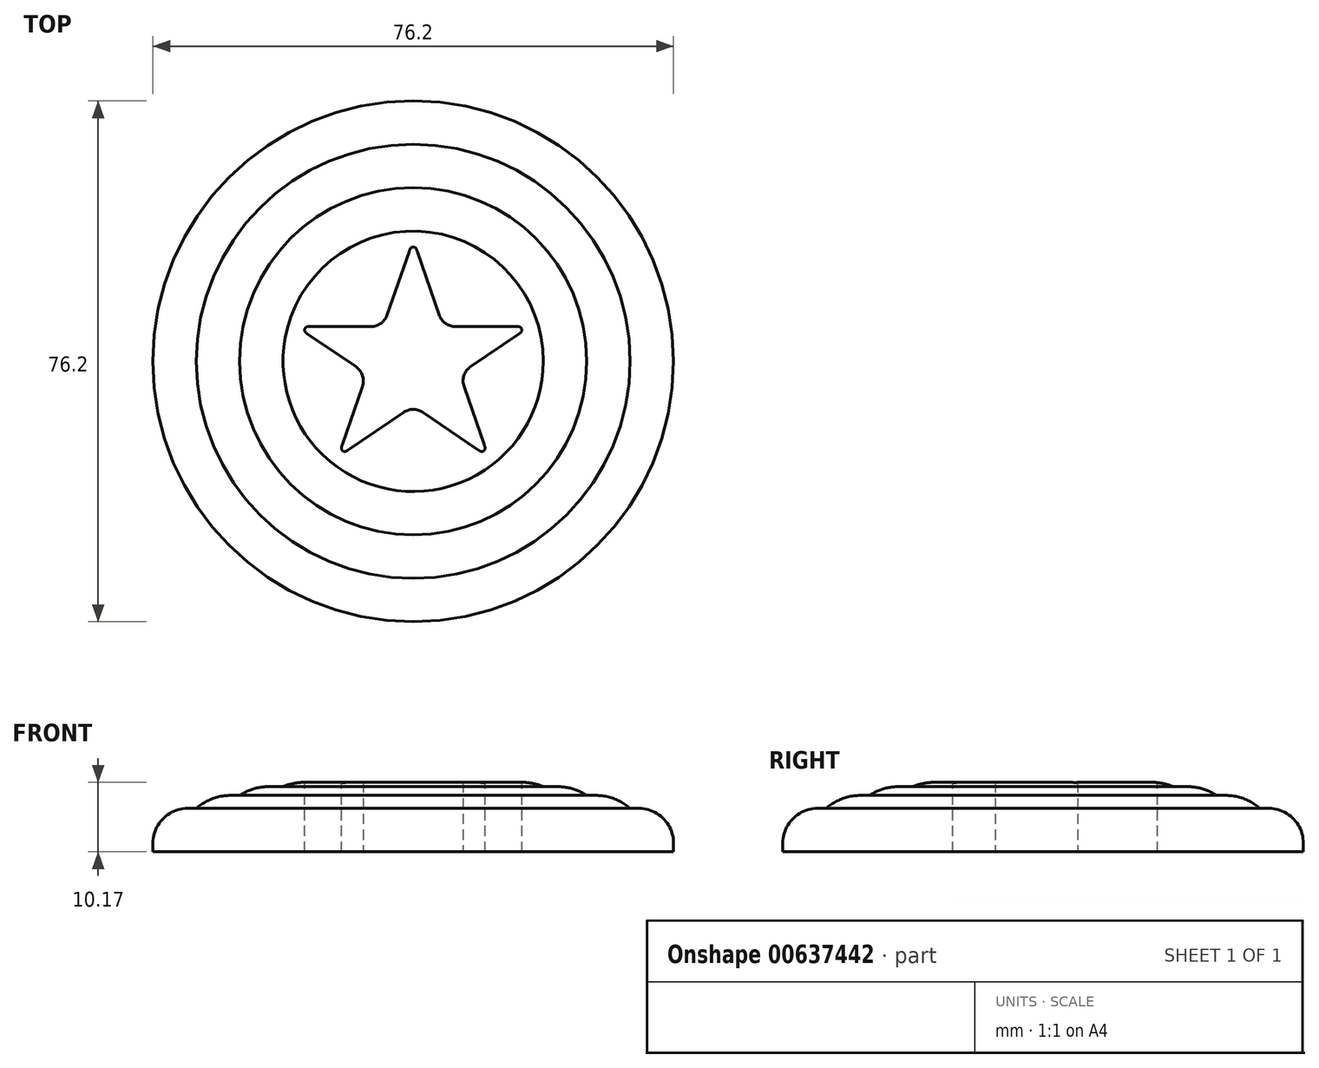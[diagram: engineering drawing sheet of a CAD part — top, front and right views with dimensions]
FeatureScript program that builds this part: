
annotation { "Feature Type Name" : "Feature", "Feature Type Description" : "" }
export const myFeature = defineFeature(function(context is Context, id is Id, definition is map)
    precondition{}
    {
        {
            var Q0;
            Q0=qCreatedBy(makeId("Top.planeOp"),FACE);
            var sketch = newSketch(context, id + "F0", { "sketchPlane" : qUnion([Q0])});
            skCircle(sketch, "E0", {"center": v(0, 0) * mm, "radius": 38.1 * mm});
            skSolve(sketch);
        }
        {
            var Q0;
            Q0 = qSketchRegion(id + "F0", true);
            extrude(context, id + "F1", {"entities" : qUnion([Q0]), "endBound" : BoundingType.SYMMETRIC, "depth" : 6.35 * mm, "offsetDistance" : 25.4 * mm});
        }
        {
            var Q0;
            Q0=makeQuery(id+"F1.opExtrude","CAP_FACE",FACE,{"disambiguationData":[OSD([sQuery(id+"F0.wireOp",EDGE,"E0")])],"isStart":false});
            var sketch = newSketch(context, id + "F2", { "sketchPlane" : qUnion([Q0])});
            skCircle(sketch, "E1", {"center": v(0, 0) * mm, "radius": 31.75 * mm, "construction": true});
            skCircle(sketch, "E2", {"center": v(0, 0) * mm, "radius": 25.4 * mm, "construction": true});
            skCircle(sketch, "E3", {"center": v(0, 0) * mm, "radius": 19.05 * mm, "construction": true});
            skLineSegment(sketch, "E4", {"start": v(0, 17.78) * mm, "end": v(0, -19.05) * mm, "construction": true});
            skLineSegment(sketch, "E5", {"start": v(0, 17.78) * mm, "end": v(-4.4, 5.08) * mm});
            skLineSegment(sketch, "E6", {"start": v(-11, -13.97) * mm, "end": v(0, -6.5) * mm});
            skLineSegment(sketch, "E7", {"start": v(17.04, 5.08) * mm, "end": v(4.4, 5.08) * mm});
            skLineSegment(sketch, "E8", {"start": v(-17.04, 5.08) * mm, "end": v(-6.8, -1.87) * mm});
            skLineSegment(sketch, "E9", {"start": v(11, -13.97) * mm, "end": v(6.8, -1.87) * mm});
            skCircle(sketch, "E10.0", {"center": v(0, 0) * mm, "radius": 38.1 * mm, "construction": true});
            skLineSegment(sketch, "E11.trimOffspring", {"start": v(-4.4, 5.08) * mm, "end": v(-17.04, 5.08) * mm});
            skLineSegment(sketch, "E12.trimOffspring", {"start": v(4.4, 5.08) * mm, "end": v(0, 17.78) * mm});
            skLineSegment(sketch, "E13.trimOffspring", {"start": v(0, -6.5) * mm, "end": v(11, -13.97) * mm});
            skLineSegment(sketch, "E14.trimOffspring", {"start": v(6.8, -1.87) * mm, "end": v(17.04, 5.08) * mm});
            skLineSegment(sketch, "E15.trimOffspring", {"start": v(-6.8, -1.87) * mm, "end": v(-11, -13.97) * mm});
            skCircle(sketch, "E16", {"center": v(0, 0) * mm, "radius": 17.78 * mm, "construction": true});
            skSolve(sketch);
        }
        {
            var Q0;
            Q0=makeQuery(id+"F1.opExtrude","CAP_FACE",FACE,{"disambiguationData":[OSD([sQuery(id+"F0.wireOp",EDGE,"E0")])],"isStart":false});
            var sketch = newSketch(context, id + "F3", { "sketchPlane" : qUnion([Q0])});
            skCircle(sketch, "E17.0", {"center": v(0, 0) * mm, "radius": 31.75 * mm});
            skCircle(sketch, "E17.1", {"center": v(0, 0) * mm, "radius": 25.4 * mm, "construction": true});
            skCircle(sketch, "E17.2", {"center": v(0, 0) * mm, "radius": 19.05 * mm, "construction": true});
            skSolve(sketch);
        }
        {
            var Q0;
            Q0 = qSketchRegion(id + "F3", true);
            extrude(context, id + "F4", {"entities" : qUnion([Q0]), "operationType" : NewBodyOperationType.ADD, "depth" : 1.9 * mm, "offsetDistance" : 25.4 * mm});
        }
        {
            var Q0;
            Q0=makeQuery(id+"F4.opExtrude","CAP_FACE",FACE,{"disambiguationData":[OSD([sQuery(id+"F3.wireOp",EDGE,"E17.0")])],"isStart":false});
            var sketch = newSketch(context, id + "F5", { "sketchPlane" : qUnion([Q0])});
            skCircle(sketch, "E18.0", {"center": v(0, 0) * mm, "radius": 25.4 * mm});
            skSolve(sketch);
        }
        {
            var Q0;
            Q0 = qSketchRegion(id + "F5", true);
            extrude(context, id + "F6", {"entities" : qUnion([Q0]), "operationType" : NewBodyOperationType.ADD, "depth" : 1.27 * mm, "offsetDistance" : 25.4 * mm});
        }
        {
            var Q0;
            Q0=makeQuery(id+"F6.opExtrude","CAP_FACE",FACE,{"disambiguationData":[OSD([sQuery(id+"F5.wireOp",EDGE,"E18.0")])],"isStart":false});
            var sketch = newSketch(context, id + "F7", { "sketchPlane" : qUnion([Q0])});
            skCircle(sketch, "E19.0", {"center": v(0, 0) * mm, "radius": 19.05 * mm});
            skSolve(sketch);
        }
        {
            var Q0;
            Q0=makeQuery(id+"F7.imprint","IMPRINT",FACE,{"disambiguationData":[TD([[makeQuery(id+"F7.imprint","IMPRINT",EDGE,{"derivedFrom":sQuery(id+"F7.wireOp",EDGE,"E19.0")}),1.0]])]});
            extrude(context, id + "F8", {"entities" : qUnion([Q0]), "operationType" : NewBodyOperationType.ADD, "depth" : 0.64 * mm, "offsetDistance" : 25.4 * mm});
        }
        {
            var Q0;
            Q0=makeQuery(id+"F1.opExtrude","CAP_FACE",FACE,{"disambiguationData":[OSD([sQuery(id+"F0.wireOp",EDGE,"E0")])],"isStart":true});
            var sketch = newSketch(context, id + "F9", { "sketchPlane" : qUnion([Q0])});
            skLineSegment(sketch, "E20.0", {"start": v(-17.04, -5.08) * mm, "end": v(-6.8, 1.87) * mm});
            skLineSegment(sketch, "E20.1", {"start": v(-6.8, 1.87) * mm, "end": v(-11, 13.97) * mm});
            skLineSegment(sketch, "E20.2", {"start": v(-11, 13.97) * mm, "end": v(0, 6.5) * mm});
            skLineSegment(sketch, "E20.3", {"start": v(0, 6.5) * mm, "end": v(11, 13.97) * mm});
            skLineSegment(sketch, "E20.4", {"start": v(11, 13.97) * mm, "end": v(6.8, 1.87) * mm});
            skLineSegment(sketch, "E20.5", {"start": v(6.8, 1.87) * mm, "end": v(17.04, -5.08) * mm});
            skLineSegment(sketch, "E20.6", {"start": v(17.04, -5.08) * mm, "end": v(4.4, -5.08) * mm});
            skLineSegment(sketch, "E20.7", {"start": v(4.4, -5.08) * mm, "end": v(0, -17.78) * mm});
            skLineSegment(sketch, "E20.8", {"start": v(0, -17.78) * mm, "end": v(-4.4, -5.08) * mm});
            skLineSegment(sketch, "E20.9", {"start": v(-4.4, -5.08) * mm, "end": v(-17.04, -5.08) * mm});
            skSolve(sketch);
        }
        {
            var Q0;
            Q0 = qSketchRegion(id + "F9", true);
            extrude(context, id + "F10", {"entities" : qUnion([Q0]), "operationType" : NewBodyOperationType.REMOVE, "endBound" : BoundingType.THROUGH_ALL, "oppositeDirection" : true, "depth" : 25.4 * mm, "offsetDistance" : 25.4 * mm});
        }
        {
            var Q0;
            Q0=makeQuery(id+"F1.opExtrude","CAP_EDGE",EDGE,{"disambiguationData":[OSD([sQuery(id+"F0.wireOp",EDGE,"E0")])],"isStart":false});
            fillet(context, id + "F11", {"entities" : qUnion([Q0]), "radius" : 5.08 * mm, "tangentPropagation" : true, "allowEdgeOverflow" : false});
        }
        {
            var Q0;
            Q0=makeQuery(id+"F4.opExtrude","CAP_EDGE",EDGE,{"disambiguationData":[OSD([sQuery(id+"F3.wireOp",EDGE,"E17.0")])],"isStart":false});
            fillet(context, id + "F12", {"entities" : qUnion([Q0]), "radius" : 7.62 * mm, "tangentPropagation" : true, "allowEdgeOverflow" : false});
        }
        {
            var Q0;
            Q0=makeQuery(id+"F6.opExtrude","CAP_EDGE",EDGE,{"disambiguationData":[OSD([sQuery(id+"F5.wireOp",EDGE,"E18.0")])],"isStart":false});
            fillet(context, id + "F13", {"entities" : qUnion([Q0]), "radius" : 7.62 * mm, "tangentPropagation" : true, "allowEdgeOverflow" : false});
        }
        {
            var Q0;
            Q0=makeQuery(id+"F8.opExtrude","CAP_EDGE",EDGE,{"disambiguationData":[OSD([sQuery(id+"F7.wireOp",EDGE,"E19.0")])],"isStart":false});
            fillet(context, id + "F14", {"entities" : qUnion([Q0]), "radius" : 7.62 * mm, "tangentPropagation" : true, "allowEdgeOverflow" : false});
        }
        {
            var Q0;
            Q0=makeQuery(id+"F10.boolean.opBoolean","COPY",EDGE,{"derivedFrom":makeQuery(id+"F10.opExtrude","SWEPT_EDGE",EDGE,{"disambiguationData":[OSD([sQuery(id+"F9.wireOp",EDGE,"E20.6"),sQuery(id+"F9.wireOp",EDGE,"E20.7")])]})});
            var Q1;
            Q1=makeQuery(id+"F10.boolean.opBoolean","COPY",EDGE,{"derivedFrom":makeQuery(id+"F10.opExtrude","SWEPT_EDGE",EDGE,{"disambiguationData":[OSD([sQuery(id+"F9.wireOp",EDGE,"E20.8"),sQuery(id+"F9.wireOp",EDGE,"E20.9")])]})});
            var Q2;
            Q2=makeQuery(id+"F10.boolean.opBoolean","COPY",EDGE,{"derivedFrom":makeQuery(id+"F10.opExtrude","SWEPT_EDGE",EDGE,{"disambiguationData":[OSD([sQuery(id+"F9.wireOp",EDGE,"E20.0"),sQuery(id+"F9.wireOp",EDGE,"E20.1")])]})});
            var Q3;
            Q3=makeQuery(id+"F10.boolean.opBoolean","COPY",EDGE,{"derivedFrom":makeQuery(id+"F10.opExtrude","SWEPT_EDGE",EDGE,{"disambiguationData":[OSD([sQuery(id+"F9.wireOp",EDGE,"E20.2"),sQuery(id+"F9.wireOp",EDGE,"E20.3")])]})});
            var Q4;
            Q4=makeQuery(id+"F10.boolean.opBoolean","COPY",EDGE,{"derivedFrom":makeQuery(id+"F10.opExtrude","SWEPT_EDGE",EDGE,{"disambiguationData":[OSD([sQuery(id+"F9.wireOp",EDGE,"E20.4"),sQuery(id+"F9.wireOp",EDGE,"E20.5")])]})});
            fillet(context, id + "F15", {"entities" : qUnion([Q0, Q1, Q2, Q3, Q4]), "radius" : 2.54 * mm, "tangentPropagation" : true, "allowEdgeOverflow" : false});
        }
        {
            var Q0;
            Q0=makeQuery(id+"F10.boolean.opBoolean","COPY",EDGE,{"derivedFrom":makeQuery(id+"F10.opExtrude","SWEPT_EDGE",EDGE,{"disambiguationData":[OSD([sQuery(id+"F9.wireOp",EDGE,"E20.1"),sQuery(id+"F9.wireOp",EDGE,"E20.2")])]})});
            var Q1;
            Q1=makeQuery(id+"F10.boolean.opBoolean","COPY",EDGE,{"derivedFrom":makeQuery(id+"F10.opExtrude","SWEPT_EDGE",EDGE,{"disambiguationData":[OSD([sQuery(id+"F9.wireOp",EDGE,"E20.0"),sQuery(id+"F9.wireOp",EDGE,"E20.9")])]})});
            var Q2;
            Q2=makeQuery(id+"F10.boolean.opBoolean","COPY",EDGE,{"derivedFrom":makeQuery(id+"F10.opExtrude","SWEPT_EDGE",EDGE,{"disambiguationData":[OSD([sQuery(id+"F9.wireOp",EDGE,"E20.7"),sQuery(id+"F9.wireOp",EDGE,"E20.8")])]})});
            var Q3;
            Q3=makeQuery(id+"F10.boolean.opBoolean","COPY",EDGE,{"derivedFrom":makeQuery(id+"F10.opExtrude","SWEPT_EDGE",EDGE,{"disambiguationData":[OSD([sQuery(id+"F9.wireOp",EDGE,"E20.5"),sQuery(id+"F9.wireOp",EDGE,"E20.6")])]})});
            var Q4;
            Q4=makeQuery(id+"F10.boolean.opBoolean","COPY",EDGE,{"derivedFrom":makeQuery(id+"F10.opExtrude","SWEPT_EDGE",EDGE,{"disambiguationData":[OSD([sQuery(id+"F9.wireOp",EDGE,"E20.3"),sQuery(id+"F9.wireOp",EDGE,"E20.4")])]})});
            fillet(context, id + "F16", {"entities" : qUnion([Q0, Q1, Q2, Q3, Q4]), "radius" : 0.5 * mm, "tangentPropagation" : true, "allowEdgeOverflow" : false});
        }
    });
